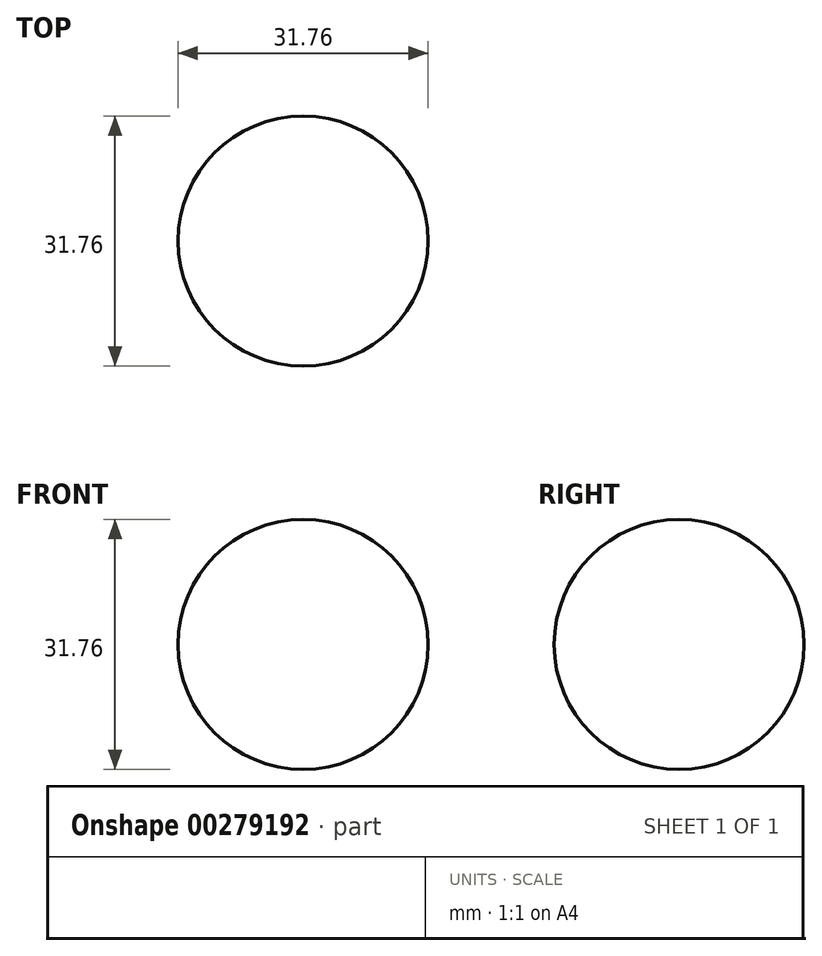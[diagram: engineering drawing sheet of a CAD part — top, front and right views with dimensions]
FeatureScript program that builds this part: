
annotation { "Feature Type Name" : "Feature", "Feature Type Description" : "" }
export const myFeature = defineFeature(function(context is Context, id is Id, definition is map)
    precondition{}
    {
        {
            var Q0;
            Q0=qCreatedBy(makeId("Top.planeOp"),FACE);
            var sketch = newSketch(context, id + "F0", { "sketchPlane" : qUnion([Q0])});
            skArc(sketch, "E0", {"start": v(0, 15.88) * mm, "mid": v(-15.88, 0) * mm, "end": v(0, -15.88) * mm});
            skLineSegment(sketch, "E1", {"start": v(0, 15.88) * mm, "end": v(0, -15.88) * mm});
            skSolve(sketch);
        }
        {
            var Q0;
            Q0=sQuery(id+"F0.wireOp",EDGE,"E0");
            var Q1;
            Q1=sQuery(id+"F0.wireOp",EDGE,"E1");
            revolve(context, id + "F1", {"bodyType" : ToolBodyType.SURFACE, "surfaceEntities" : qUnion([Q0]), "axis" : qUnion([Q1]), "revolveType" : RevolveType.FULL});
        }
    });
